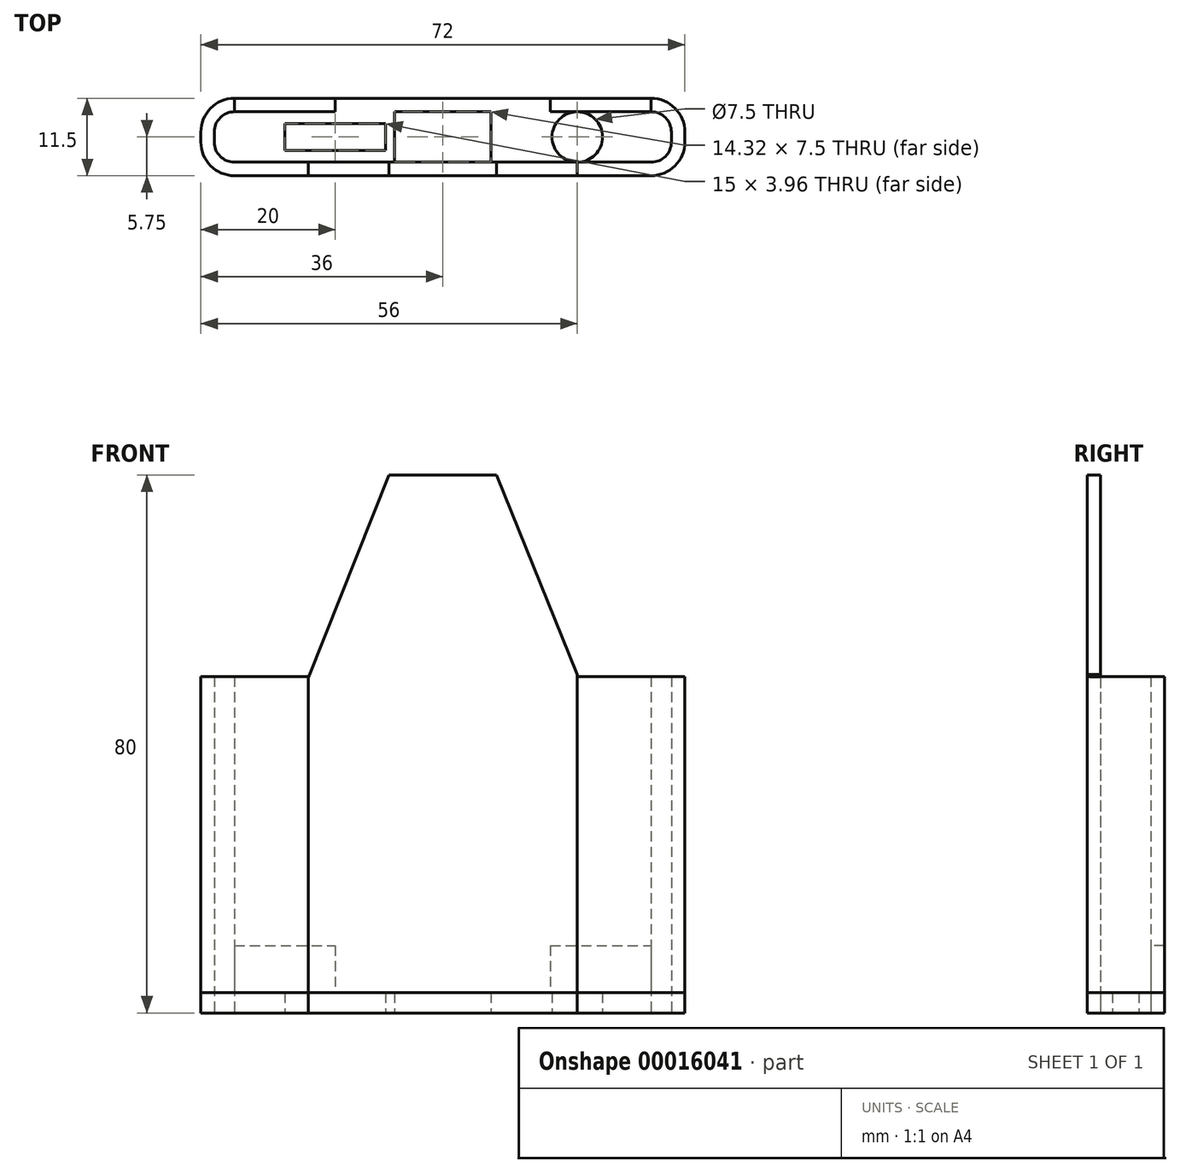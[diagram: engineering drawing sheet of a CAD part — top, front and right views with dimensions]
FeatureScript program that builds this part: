
annotation { "Feature Type Name" : "Feature", "Feature Type Description" : "" }
export const myFeature = defineFeature(function(context is Context, id is Id, definition is map)
    precondition{}
    {
        {
            var Q0;
            Q0=qCreatedBy(makeId("Top.planeOp"),FACE);
            var sketch = newSketch(context, id + "F0", { "sketchPlane" : qUnion([Q0])});
            skLineSegment(sketch, "E0.rect.bottom", {"start": v(36, -5.75) * mm, "end": v(-36, -5.75) * mm});
            skLineSegment(sketch, "E0.rect.top", {"start": v(31, 5.75) * mm, "end": v(31, 5.75) * mm});
            skLineSegment(sketch, "E0.rect.left", {"start": v(36, -5.75) * mm, "end": v(36, 0.75) * mm});
            skLineSegment(sketch, "E0.rect.right", {"start": v(-36, -5.75) * mm, "end": v(-36, 0.75) * mm});
            skPoint(sketch, "E0.rect.middle", {"position": v(0, 0) * mm});
            skLineSegment(sketch, "E1.rect.bottom", {"start": v(31, -3.75) * mm, "end": v(-31, -3.75) * mm});
            skLineSegment(sketch, "E1.rect.left", {"start": v(34, -0.75) * mm, "end": v(34, 0.75) * mm});
            skLineSegment(sketch, "E1.rect.right", {"start": v(-34, -0.75) * mm, "end": v(-34, 0.75) * mm});
            skLineSegment(sketch, "E2", {"start": v(-31, 5.75) * mm, "end": v(-31, 3.75) * mm});
            skLineSegment(sketch, "E3", {"start": v(31, 5.75) * mm, "end": v(31, 3.75) * mm});
            skPoint(sketch, "E4.visualSharp", {"position": v(-34, 3.75) * mm});
            skArc(sketch, "E4.filletArc", {"start": v(-31, 3.75) * mm, "mid": v(-33.12, 2.87) * mm, "end": v(-34, 0.75) * mm});
            skPoint(sketch, "E5.visualSharp", {"position": v(-34, -3.75) * mm});
            skArc(sketch, "E5.filletArc", {"start": v(-34, -0.75) * mm, "mid": v(-33.12, -2.87) * mm, "end": v(-31, -3.75) * mm});
            skPoint(sketch, "E6.visualSharp", {"position": v(34, -3.75) * mm});
            skArc(sketch, "E6.filletArc", {"start": v(31, -3.75) * mm, "mid": v(33.12, -2.87) * mm, "end": v(34, -0.75) * mm});
            skPoint(sketch, "E7.visualSharp", {"position": v(34, 3.75) * mm});
            skArc(sketch, "E7.filletArc", {"start": v(34, 0.75) * mm, "mid": v(33.12, 2.87) * mm, "end": v(31, 3.75) * mm});
            skLineSegment(sketch, "E8.trimOffspring", {"start": v(-31, 5.75) * mm, "end": v(-31, 5.75) * mm});
            skPoint(sketch, "E9.visualSharp", {"position": v(-36, 5.75) * mm});
            skArc(sketch, "E9.filletArc", {"start": v(-31, 5.75) * mm, "mid": v(-34.54, 4.29) * mm, "end": v(-36, 0.75) * mm});
            skPoint(sketch, "E10.visualSharp", {"position": v(36, 5.75) * mm});
            skArc(sketch, "E10.filletArc", {"start": v(36, 0.75) * mm, "mid": v(34.54, 4.29) * mm, "end": v(31, 5.75) * mm});
            skLineSegment(sketch, "E11", {"start": v(-31, 3.75) * mm, "end": v(31, 3.75) * mm});
            skLineSegment(sketch, "E12", {"start": v(-31, 5.75) * mm, "end": v(31, 5.75) * mm});
            skPoint(sketch, "E13.orphan", {"position": v(-34, 0) * mm});
            skPoint(sketch, "E14.end.orphan", {"position": v(34, 0) * mm});
            skLineSegment(sketch, "E15", {"start": v(-34, 0) * mm, "end": v(16.25, 0) * mm});
            skLineSegment(sketch, "E16.rect.bottom", {"start": v(5, -3.75) * mm, "end": v(-5, -3.75) * mm});
            skLineSegment(sketch, "E16.rect.top", {"start": v(5, 3.75) * mm, "end": v(-5, 3.75) * mm});
            skLineSegment(sketch, "E16.rect.left", {"start": v(5, -3.75) * mm, "end": v(5, 3.75) * mm});
            skLineSegment(sketch, "E16.rect.right", {"start": v(-5, -3.75) * mm, "end": v(-5, 3.75) * mm});
            skPoint(sketch, "E17.rect.middle", {"position": v(15, 0) * mm});
            skLineSegment(sketch, "E18", {"start": v(-16, 5.75) * mm, "end": v(-16, 3.75) * mm});
            skLineSegment(sketch, "E19", {"start": v(16, 5.75) * mm, "end": v(16, 3.75) * mm});
            skLineSegment(sketch, "E20", {"start": v(-20, -3.75) * mm, "end": v(-20, -5.75) * mm});
            skLineSegment(sketch, "E21", {"start": v(20, -3.75) * mm, "end": v(20, -5.75) * mm});
            skPoint(sketch, "E22.end.orphan", {"position": v(0, -5.75) * mm});
            skPoint(sketch, "E22.start.orphan", {"position": v(0, -3.75) * mm});
            skCircle(sketch, "E23", {"center": v(20, 0) * mm, "radius": 2.52 * mm});
            skLineSegment(sketch, "E24.rect.bottom", {"start": v(-8.5, -1.98) * mm, "end": v(-23.5, -1.98) * mm});
            skLineSegment(sketch, "E24.rect.top", {"start": v(-8.5, 1.98) * mm, "end": v(-23.5, 1.98) * mm});
            skLineSegment(sketch, "E24.rect.left", {"start": v(-8.5, -1.98) * mm, "end": v(-8.5, 1.98) * mm});
            skLineSegment(sketch, "E24.rect.right", {"start": v(-23.5, -1.98) * mm, "end": v(-23.5, 1.98) * mm});
            skPoint(sketch, "E24.rect.middle", {"position": v(-16, 0) * mm});
            skCircle(sketch, "E25", {"center": v(20, 0) * mm, "radius": 3.75 * mm});
            skLineSegment(sketch, "E26.rect.bottom", {"start": v(7.16, 5) * mm, "end": v(-7.16, 5) * mm});
            skLineSegment(sketch, "E26.rect.top", {"start": v(7.16, -5) * mm, "end": v(-7.16, -5) * mm});
            skLineSegment(sketch, "E26.rect.left", {"start": v(7.16, 5) * mm, "end": v(7.16, -5) * mm});
            skLineSegment(sketch, "E26.rect.right", {"start": v(-7.16, 5) * mm, "end": v(-7.16, -5) * mm});
            skLineSegment(sketch, "E27.trimOffspring", {"start": v(23.75, 0) * mm, "end": v(34, 0) * mm});
            skSolve(sketch);
        }
        {
            var Q0;
            Q0=makeQuery(id+"F0.imprint","IMPRINT",FACE,{"disambiguationData":[TD([[makeQuery(id+"F0.imprint","IMPRINT",EDGE,{"derivedFrom":sQuery(id+"F0.wireOp",EDGE,"E0.rect.bottom")}),-1.0]])]});
            var Q1;
            Q1=makeQuery(id+"F0.imprint","IMPRINT",FACE,{"disambiguationData":[TD([[makeQuery(id+"F0.imprint","IMPRINT",EDGE,{"derivedFrom":sQuery(id+"F0.wireOp",EDGE,"E2")}),1.0]])]});
            var Q2;
            {var subQ2=sQuery(id+"F0.wireOp",EDGE,"E4.filletArc");Q2=makeQuery(id+"F0.imprint","IMPRINT",FACE,{"disambiguationData":[TD([[makeQuery(id+"F0.imprint","IMPRINT",EDGE,{"derivedFrom":subQ2}),1.0]])]});}
            var Q3;
            Q3=makeQuery(id+"F0.imprint","IMPRINT",FACE,{"disambiguationData":[TD([[makeQuery(id+"F0.imprint","IMPRINT",EDGE,{"derivedFrom":sQuery(id+"F0.wireOp",EDGE,"E1.rect.bottom")}),-1.0]])]});
            var Q4;
            {var subQ2=sQuery(id+"F0.wireOp",EDGE,"E3");Q4=makeQuery(id+"F0.imprint","IMPRINT",FACE,{"disambiguationData":[TD([[makeQuery(id+"F0.imprint","IMPRINT",EDGE,{"derivedFrom":subQ2}),-1.0]])]});}
            var Q5;
            {var subQ1=sQuery(id+"F0.wireOp",EDGE,"E18");Q5=makeQuery(id+"F0.imprint","IMPRINT",FACE,{"disambiguationData":[TD([[makeQuery(id+"F0.imprint","IMPRINT",EDGE,{"derivedFrom":subQ1}),1.0]])]});}
            var Q6;
            {var subQ6=sQuery(id+"F0.wireOp",EDGE,"E0.rect.right");Q6=makeQuery(id+"F0.imprint","IMPRINT",FACE,{"disambiguationData":[TD([[makeQuery(id+"F0.imprint","IMPRINT",EDGE,{"derivedFrom":subQ6}),-1.0]])]});}
            var Q7;
            {var subQ6=sQuery(id+"F0.wireOp",EDGE,"E0.rect.left");Q7=makeQuery(id+"F0.imprint","IMPRINT",FACE,{"disambiguationData":[TD([[makeQuery(id+"F0.imprint","IMPRINT",EDGE,{"derivedFrom":subQ6}),1.0]])]});}
            var Q8;
            {var subQ7=sQuery(id+"F0.wireOp",EDGE,"E6.filletArc");Q8=makeQuery(id+"F0.imprint","IMPRINT",FACE,{"disambiguationData":[TD([[makeQuery(id+"F0.imprint","IMPRINT",EDGE,{"derivedFrom":subQ7}),1.0]])]});}
            var Q9;
            {var subQ7=sQuery(id+"F0.wireOp",EDGE,"E7.filletArc");Q9=makeQuery(id+"F0.imprint","IMPRINT",FACE,{"disambiguationData":[TD([[makeQuery(id+"F0.imprint","IMPRINT",EDGE,{"derivedFrom":subQ7}),1.0]])]});}
            var Q10;
            {var subQ0=sQuery(id+"F0.wireOp",EDGE,"E25");var subQ3=sQuery(id+"F0.wireOp",EDGE,"E11");var subQ4=makeQuery(id+"F0.imprint","INTERSECT",VERTEX,{"disambiguationData":[OD(0.0)],"derivedFrom":[subQ3,subQ0]});Q10=makeQuery(id+"F0.imprint","IMPRINT",FACE,{"disambiguationData":[TD([[makeQuery(id+"F0.imprint","IMPRINT",EDGE,{"disambiguationData":[TD([[subQ4,-1.0]])],"derivedFrom":subQ3}),-1.0]])]});}
            var Q11;
            {var subQ3=sQuery(id+"F0.wireOp",EDGE,"E11");var subQ8=makeQuery(id+"F0.imprint","INTERSECT",VERTEX,{"derivedFrom":[subQ3,sQuery(id+"F0.wireOp",EDGE,"E19")]});Q11=makeQuery(id+"F0.imprint","IMPRINT",FACE,{"disambiguationData":[TD([[makeQuery(id+"F0.imprint","IMPRINT",EDGE,{"disambiguationData":[TD([[subQ8,1.0]])],"derivedFrom":subQ3}),-1.0]])]});}
            var Q12;
            {var subQ3=sQuery(id+"F0.wireOp",EDGE,"E1.rect.bottom");var subQ5=sQuery(id+"F0.wireOp",EDGE,"E25");var subQ7=makeQuery(id+"F0.imprint","INTERSECT",VERTEX,{"disambiguationData":[OD(1.0)],"derivedFrom":[subQ3,subQ5]});Q12=makeQuery(id+"F0.imprint","IMPRINT",FACE,{"disambiguationData":[TD([[makeQuery(id+"F0.imprint","IMPRINT",EDGE,{"disambiguationData":[TD([[subQ7,-1.0]])],"derivedFrom":subQ3}),-1.0]])]});}
            var Q13;
            {var subQ7=sQuery(id+"F0.wireOp",EDGE,"E16.rect.bottom");Q13=makeQuery(id+"F0.imprint","IMPRINT",FACE,{"disambiguationData":[TD([[makeQuery(id+"F0.imprint","IMPRINT",EDGE,{"derivedFrom":subQ7}),1.0]])]});}
            var Q14;
            {var subQ7=sQuery(id+"F0.wireOp",EDGE,"E16.rect.top");Q14=makeQuery(id+"F0.imprint","IMPRINT",FACE,{"disambiguationData":[TD([[makeQuery(id+"F0.imprint","IMPRINT",EDGE,{"derivedFrom":subQ7}),-1.0]])]});}
            var Q15;
            {var subQ8=sQuery(id+"F0.wireOp",EDGE,"E5.filletArc");Q15=makeQuery(id+"F0.imprint","IMPRINT",FACE,{"disambiguationData":[TD([[makeQuery(id+"F0.imprint","IMPRINT",EDGE,{"derivedFrom":subQ8}),1.0]])]});}
            var Q16;
            {var subQ1=sQuery(id+"F0.wireOp",EDGE,"E21");var subQ3=sQuery(id+"F0.wireOp",EDGE,"E1.rect.bottom");var subQ5=makeQuery(id+"F0.imprint","INTERSECT",VERTEX,{"derivedFrom":[subQ3,subQ1]});Q16=makeQuery(id+"F0.imprint","IMPRINT",FACE,{"disambiguationData":[TD([[makeQuery(id+"F0.imprint","IMPRINT",EDGE,{"disambiguationData":[TD([[subQ5,1.0]])],"derivedFrom":subQ3}),1.0]])]});}
            var Q17;
            {var subQ1=sQuery(id+"F0.wireOp",EDGE,"E21");var subQ3=sQuery(id+"F0.wireOp",EDGE,"E1.rect.bottom");var subQ5=makeQuery(id+"F0.imprint","INTERSECT",VERTEX,{"derivedFrom":[subQ3,subQ1]});Q17=makeQuery(id+"F0.imprint","IMPRINT",FACE,{"disambiguationData":[TD([[makeQuery(id+"F0.imprint","IMPRINT",EDGE,{"disambiguationData":[TD([[subQ5,-1.0]])],"derivedFrom":subQ3}),1.0]])]});}
            var Q18;
            {var subQ0=sQuery(id+"F0.wireOp",EDGE,"E25");var subQ1=sQuery(id+"F0.wireOp",EDGE,"E11");var subQ3=makeQuery(id+"F0.imprint","INTERSECT",VERTEX,{"disambiguationData":[OD(0.0)],"derivedFrom":[subQ1,subQ0]});Q18=makeQuery(id+"F0.imprint","IMPRINT",FACE,{"disambiguationData":[TD([[makeQuery(id+"F0.imprint","IMPRINT",EDGE,{"disambiguationData":[TD([[subQ3,-1.0]])],"derivedFrom":subQ1}),1.0]])]});}
            var Q19;
            {var subQ3=sQuery(id+"F0.wireOp",EDGE,"E26.rect.bottom");Q19=makeQuery(id+"F0.imprint","IMPRINT",FACE,{"disambiguationData":[TD([[makeQuery(id+"F0.imprint","IMPRINT",EDGE,{"derivedFrom":subQ3}),1.0]])]});}
            var Q20;
            {var subQ3=sQuery(id+"F0.wireOp",EDGE,"E26.rect.top");Q20=makeQuery(id+"F0.imprint","IMPRINT",FACE,{"disambiguationData":[TD([[makeQuery(id+"F0.imprint","IMPRINT",EDGE,{"derivedFrom":subQ3}),-1.0]])]});}
            extrude(context, id + "F1", {"entities" : qUnion([Q0, Q1, Q2, Q3, Q4, Q5, Q6, Q7, Q8, Q9, Q10, Q11, Q12, Q13, Q14, Q15, Q16, Q17, Q18, Q19, Q20]), "depth" : 3 * mm});
        }
        {
            var Q0;
            Q0=makeQuery(id+"F0.imprint","IMPRINT",FACE,{"disambiguationData":[TD([[makeQuery(id+"F0.imprint","IMPRINT",EDGE,{"derivedFrom":sQuery(id+"F0.wireOp",EDGE,"E0.rect.bottom")}),-1.0]])]});
            var Q1;
            {var subQ3=sQuery(id+"F0.wireOp",EDGE,"E26.rect.top");Q1=makeQuery(id+"F0.imprint","IMPRINT",FACE,{"disambiguationData":[TD([[makeQuery(id+"F0.imprint","IMPRINT",EDGE,{"derivedFrom":subQ3}),-1.0]])]});}
            var Q2;
            {var subQ1=sQuery(id+"F0.wireOp",EDGE,"E21");var subQ3=sQuery(id+"F0.wireOp",EDGE,"E1.rect.bottom");var subQ5=makeQuery(id+"F0.imprint","INTERSECT",VERTEX,{"derivedFrom":[subQ3,subQ1]});Q2=makeQuery(id+"F0.imprint","IMPRINT",FACE,{"disambiguationData":[TD([[makeQuery(id+"F0.imprint","IMPRINT",EDGE,{"disambiguationData":[TD([[subQ5,-1.0]])],"derivedFrom":subQ3}),1.0]])]});}
            extrude(context, id + "F2", {"entities" : qUnion([Q0, Q1, Q2]), "depth" : 80 * mm});
        }
        {
            var Q0;
            {var subQ2=sQuery(id+"F0.wireOp",EDGE,"E3");Q0=makeQuery(id+"F0.imprint","IMPRINT",FACE,{"disambiguationData":[TD([[makeQuery(id+"F0.imprint","IMPRINT",EDGE,{"derivedFrom":subQ2}),-1.0]])]});}
            var Q1;
            {var subQ2=sQuery(id+"F0.wireOp",EDGE,"E2");Q1=makeQuery(id+"F0.imprint","IMPRINT",FACE,{"disambiguationData":[TD([[makeQuery(id+"F0.imprint","IMPRINT",EDGE,{"derivedFrom":subQ2}),1.0]])]});}
            extrude(context, id + "F3", {"entities" : qUnion([Q0, Q1]), "operationType" : NewBodyOperationType.ADD, "depth" : 10 * mm});
        }
        {
            var Q0;
            {var subQ6=sQuery(id+"F0.wireOp",EDGE,"E0.rect.left");Q0=makeQuery(id+"F0.imprint","IMPRINT",FACE,{"disambiguationData":[TD([[makeQuery(id+"F0.imprint","IMPRINT",EDGE,{"derivedFrom":subQ6}),1.0]])]});}
            var Q1;
            {var subQ6=sQuery(id+"F0.wireOp",EDGE,"E0.rect.right");Q1=makeQuery(id+"F0.imprint","IMPRINT",FACE,{"disambiguationData":[TD([[makeQuery(id+"F0.imprint","IMPRINT",EDGE,{"derivedFrom":subQ6}),-1.0]])]});}
            extrude(context, id + "F4", {"entities" : qUnion([Q0, Q1]), "depth" : 50 * mm});
        }
        {
            var Q0;
            Q0=makeQuery(id+"F2.opExtrude","SWEPT_FACE",FACE,{"disambiguationData":[OSD([sQuery(id+"F0.wireOp",EDGE,"E0.rect.bottom")])]});
            var sketch = newSketch(context, id + "F5", { "sketchPlane" : qUnion([Q0])});
            skLineSegment(sketch, "E28", {"start": v(-20, 49.82) * mm, "end": v(-8, 80) * mm});
            skLineSegment(sketch, "E29", {"start": v(20, 50.33) * mm, "end": v(8, 80) * mm});
            skLineSegment(sketch, "E30.rect.bottom", {"start": v(10, 25) * mm, "end": v(-10, 25) * mm});
            skLineSegment(sketch, "E30.rect.top", {"start": v(10, 45) * mm, "end": v(-10, 45) * mm});
            skLineSegment(sketch, "E30.rect.left", {"start": v(10, 25) * mm, "end": v(10, 45) * mm});
            skLineSegment(sketch, "E30.rect.right", {"start": v(-10, 25) * mm, "end": v(-10, 45) * mm});
            skPoint(sketch, "E30.rect.middle", {"position": v(0, 35) * mm});
            skCircle(sketch, "E31", {"center": v(-10, 45) * mm, "radius": 3 * mm});
            skCircle(sketch, "E32", {"center": v(10, 45) * mm, "radius": 3 * mm});
            skCircle(sketch, "E33", {"center": v(9.87, 25.03) * mm, "radius": 3 * mm});
            skCircle(sketch, "E34", {"center": v(-10, 25.03) * mm, "radius": 3 * mm});
            skSolve(sketch);
        }
        {
            var Q0;
            Q0=makeQuery(id+"F4.opExtrude","SWEPT_EDGE",EDGE,{"disambiguationData":[OSD([sQuery(id+"F0.wireOp",EDGE,"E0.rect.bottom"),sQuery(id+"F0.wireOp",EDGE,"E0.rect.right")])]});
            var Q1;
            Q1=makeQuery(id+"F4.opExtrude","SWEPT_EDGE",EDGE,{"disambiguationData":[OSD([sQuery(id+"F0.wireOp",EDGE,"E0.rect.bottom"),sQuery(id+"F0.wireOp",EDGE,"E0.rect.left")])]});
            var Q2;
            Q2=makeQuery(id+"F1.opExtrude","SWEPT_EDGE",EDGE,{"disambiguationData":[OSD([sQuery(id+"F0.wireOp",EDGE,"E0.rect.bottom"),sQuery(id+"F0.wireOp",EDGE,"E0.rect.right")])]});
            var Q3;
            Q3=makeQuery(id+"F1.opExtrude","SWEPT_EDGE",EDGE,{"disambiguationData":[OSD([sQuery(id+"F0.wireOp",EDGE,"E0.rect.bottom"),sQuery(id+"F0.wireOp",EDGE,"E0.rect.left")])]});
            fillet(context, id + "F6", {"entities" : qUnion([Q0, Q1, Q2, Q3]), "radius" : 5 * mm, "tangentPropagation" : true, "allowEdgeOverflow" : false});
        }
        {
            var Q0;
            {var subQ2=sQuery(id+"F5.wireOp",EDGE,"E29");Q0=makeQuery(id+"F5.imprint","IMPRINT",FACE,{"disambiguationData":[TD([[makeQuery(id+"F5.imprint","IMPRINT",EDGE,{"derivedFrom":subQ2}),-1.0]])]});}
            var Q1;
            {var subQ2=sQuery(id+"F5.wireOp",EDGE,"E28");Q1=makeQuery(id+"F5.imprint","IMPRINT",FACE,{"disambiguationData":[TD([[makeQuery(id+"F5.imprint","IMPRINT",EDGE,{"derivedFrom":subQ2}),1.0]])]});}
            extrude(context, id + "F7", {"entities" : qUnion([Q0, Q1]), "operationType" : NewBodyOperationType.REMOVE, "endBound" : BoundingType.THROUGH_ALL, "oppositeDirection" : true, "depth" : 25 * mm});
        }
    });
